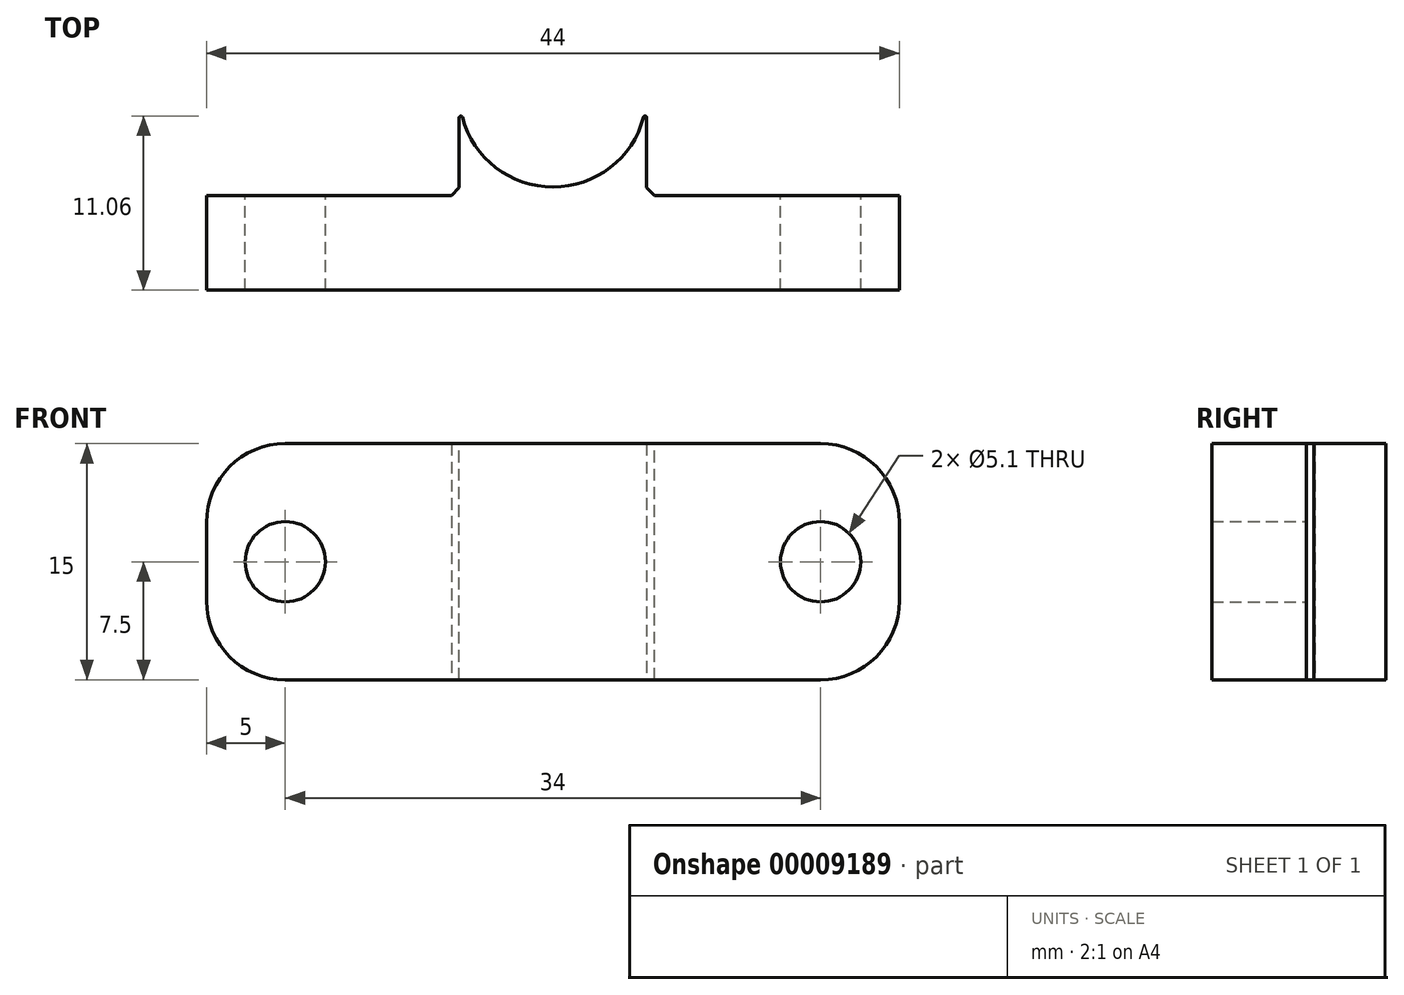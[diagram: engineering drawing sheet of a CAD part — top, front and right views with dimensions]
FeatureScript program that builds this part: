
annotation { "Feature Type Name" : "Feature", "Feature Type Description" : "" }
export const myFeature = defineFeature(function(context is Context, id is Id, definition is map)
    precondition{}
    {
        {
            var Q0;
            Q0=qCreatedBy(makeId("Top.planeOp"),FACE);
            var sketch = newSketch(context, id + "F0", { "sketchPlane" : qUnion([Q0])});
            skArc(sketch, "E0", {"start": v(-5.95, 0) * mm, "mid": v(0, -5.95) * mm, "end": v(5.95, 0) * mm});
            skLineSegment(sketch, "E1", {"start": v(-5.95, -6.5) * mm, "end": v(-5.95, 0) * mm});
            skLineSegment(sketch, "E2", {"start": v(5.95, -6.5) * mm, "end": v(22, -6.5) * mm});
            skLineSegment(sketch, "E3", {"start": v(22, -6.5) * mm, "end": v(22, -12.5) * mm});
            skLineSegment(sketch, "E4", {"start": v(22, -12.5) * mm, "end": v(-22, -12.5) * mm});
            skLineSegment(sketch, "E5", {"start": v(-22, -12.5) * mm, "end": v(-22, -6.5) * mm});
            skLineSegment(sketch, "E6", {"start": v(-22, -6.5) * mm, "end": v(-5.95, -6.5) * mm});
            skLineSegment(sketch, "E7.trimOffspring", {"start": v(5.95, -6.5) * mm, "end": v(5.95, 0) * mm});
            skSolve(sketch);
        }
        {
            var Q0;
            Q0=makeQuery(id+"F0.imprint","IMPRINT",FACE,{"disambiguationData":[TD([[makeQuery(id+"F0.imprint","IMPRINT",EDGE,{"derivedFrom":sQuery(id+"F0.wireOp",EDGE,"E0")}),-1.0]])]});
            extrude(context, id + "F1", {"entities" : qUnion([Q0]), "depth" : 15 * mm});
        }
        {
            var Q0;
            Q0=makeQuery(id+"F1.opExtrude","SWEPT_FACE",FACE,{"disambiguationData":[OSD([sQuery(id+"F0.wireOp",EDGE,"E2")])]});
            var sketch = newSketch(context, id + "F2", { "sketchPlane" : qUnion([Q0])});
            skCircle(sketch, "E8", {"center": v(-17, 7.5) * mm, "radius": 2.55 * mm});
            skCircle(sketch, "E9", {"center": v(17, 7.5) * mm, "radius": 2.55 * mm});
            skSolve(sketch);
        }
        {
            var Q0;
            Q0=makeQuery(id+"F2.imprint","IMPRINT",FACE,{"disambiguationData":[TD([[makeQuery(id+"F2.imprint","IMPRINT",EDGE,{"derivedFrom":sQuery(id+"F2.wireOp",EDGE,"E8")}),1.0]])]});
            var Q1;
            Q1=makeQuery(id+"F2.imprint","IMPRINT",FACE,{"disambiguationData":[TD([[makeQuery(id+"F2.imprint","IMPRINT",EDGE,{"derivedFrom":sQuery(id+"F2.wireOp",EDGE,"E9")}),1.0]])]});
            extrude(context, id + "F3", {"entities" : qUnion([Q0, Q1]), "operationType" : NewBodyOperationType.REMOVE, "endBound" : BoundingType.THROUGH_ALL, "oppositeDirection" : true, "depth" : 25 * mm});
        }
        {
            var Q0;
            Q0=makeQuery(id+"F1.opExtrude","CAP_EDGE",EDGE,{"disambiguationData":[OSD([sQuery(id+"F0.wireOp",EDGE,"E5")])],"isStart":false});
            var Q1;
            Q1=makeQuery(id+"F1.opExtrude","CAP_EDGE",EDGE,{"disambiguationData":[OSD([sQuery(id+"F0.wireOp",EDGE,"E5")])],"isStart":true});
            var Q2;
            Q2=makeQuery(id+"F1.opExtrude","CAP_EDGE",EDGE,{"disambiguationData":[OSD([sQuery(id+"F0.wireOp",EDGE,"E3")])],"isStart":false});
            var Q3;
            Q3=makeQuery(id+"F1.opExtrude","CAP_EDGE",EDGE,{"disambiguationData":[OSD([sQuery(id+"F0.wireOp",EDGE,"E3")])],"isStart":true});
            fillet(context, id + "F4", {"entities" : qUnion([Q0, Q1, Q2, Q3]), "radius" : 5 * mm, "tangentPropagation" : true, "allowEdgeOverflow" : false});
        }
        {
            var Q0;
            Q0=makeQuery(id+"F1.opExtrude","SWEPT_EDGE",EDGE,{"disambiguationData":[OSD([sQuery(id+"F0.wireOp",EDGE,"E0"),sQuery(id+"F0.wireOp",EDGE,"E7.trimOffspring")])]});
            var Q1;
            Q1=makeQuery(id+"F1.opExtrude","SWEPT_EDGE",EDGE,{"disambiguationData":[OSD([sQuery(id+"F0.wireOp",EDGE,"E0"),sQuery(id+"F0.wireOp",EDGE,"E1")])]});
            fillet(context, id + "F5", {"entities" : qUnion([Q0, Q1]), "radius" : .1 * mm, "tangentPropagation" : true, "allowEdgeOverflow" : false});
        }
        {
            var Q0;
            Q0=makeQuery(id+"F1.opExtrude","SWEPT_EDGE",EDGE,{"disambiguationData":[OSD([sQuery(id+"F0.wireOp",EDGE,"E1"),sQuery(id+"F0.wireOp",EDGE,"E6")])]});
            var Q1;
            Q1=makeQuery(id+"F1.opExtrude","SWEPT_EDGE",EDGE,{"disambiguationData":[OSD([sQuery(id+"F0.wireOp",EDGE,"E2"),sQuery(id+"F0.wireOp",EDGE,"E7.trimOffspring")])]});
            chamfer(context, id + "F6", {"entities" : qUnion([Q0, Q1]), "width" : .5 * mm, "tangentPropagation" : true});
        }
    });
